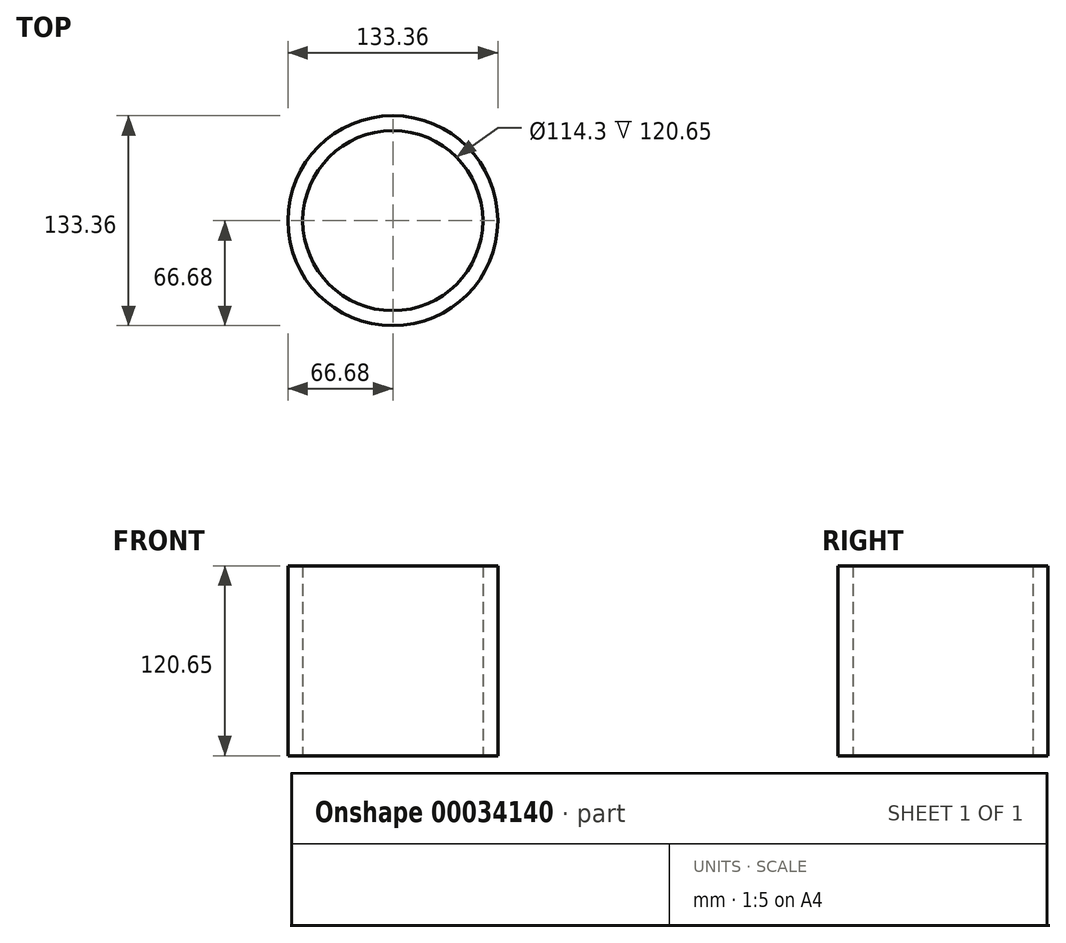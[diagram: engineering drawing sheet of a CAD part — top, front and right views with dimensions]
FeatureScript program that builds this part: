
annotation { "Feature Type Name" : "Feature", "Feature Type Description" : "" }
export const myFeature = defineFeature(function(context is Context, id is Id, definition is map)
    precondition{}
    {
        {
            var Q0;
            Q0=qCreatedBy(makeId("Top.planeOp"),FACE);
            var sketch = newSketch(context, id + "F0", { "sketchPlane" : qUnion([Q0])});
            skCircle(sketch, "E0", {"center": v(0, 0) * mm, "radius": 66.68 * mm});
            skSolve(sketch);
        }
        {
            var Q0;
            Q0 = qSketchRegion(id + "F0", true);
            extrude(context, id + "F1", {"entities" : qUnion([Q0]), "depth" : 120.65 * mm});
        }
        {
            var Q0;
            Q0=qCreatedBy(makeId("Top.planeOp"),FACE);
            var sketch = newSketch(context, id + "F2", { "sketchPlane" : qUnion([Q0])});
            skCircle(sketch, "E1", {"center": v(0, 0) * mm, "radius": 57.15 * mm});
            skSolve(sketch);
        }
        {
            var Q0;
            Q0=makeQuery(id+"F2.imprint","IMPRINT",FACE,{"disambiguationData":[TD([[makeQuery(id+"F2.imprint","IMPRINT",EDGE,{"derivedFrom":sQuery(id+"F2.wireOp",EDGE,"E1")}),1.0]])]});
            extrude(context, id + "F3", {"entities" : qUnion([Q0]), "operationType" : NewBodyOperationType.REMOVE, "depth" : 152.4 * mm});
        }
    });
